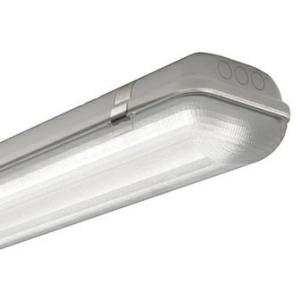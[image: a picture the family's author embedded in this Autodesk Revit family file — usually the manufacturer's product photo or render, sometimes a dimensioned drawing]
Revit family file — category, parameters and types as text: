
# Revit family: 3f_filippi_-_3f_linda_3f_filippi_-_58569_-_3f_linda_led_1x6w_ep_la_l660
name_source: partatom
category: Lighting Fixtures
units: mm (PartAtom-declared; Revit-internal decimal feet)

## family parameters
Cut with Voids When Loaded = No
Host = Face
Light Source = No
Part Type = Normal
Room Calculation Point = No
Round Connector Dimension = Use Diameter
Shared = No

## types (1)
- 3F Filippi - 3F Linda (1 x LED, 1029 lm, 8.5 W, 4000 K)
    Apparent Load = 9 VA
    Approval mark = ENEC
    CIE Flux Codes = 44 77 94 97 100
    Color Rendering = 80
    Color Temperature = 4000 K
    Control Gear = Electronic ballast
    Default Elevation = 1800 mm
    Description = ILLUMINOTECHNICAL
Luminous efficiency 100% (DLOR 97%, ULOR 3%).
Initial luminous flux of the luminaire 1029 lm.
Emergency luminaire luminous flux BLF 57.1%.
Controlled direct symmetric distribution.
Installation Interdistance Transv.D = 1.77 x hu - Long.D = 1.17 x hu.
Tabular UGR (CIE 117 - 4H-8H; S=0.25H; 70/50/20): RUG 18.5 - 18.9.
Beam angle: 109° - 64°.
Luminous efficacy 121 lm/W.
Lifetime (L93/B10): 30000 h. (tq+25°C)
Lifetime (L90/B10): 50000 h. (tq+25°C)
Lifetime (L85/B10): 80000 h. (tq+25°C)
Lifetime (L80/B10): 100000 h. (tq+25°C)
Sudden decreased luminous flux after 50000 hours: 0% (C0).
Photobiological safety in compliance with IEC/TR 62778: RG0 risk exempt, (IEC 62471).
In compliance with IEC/EN 62722-2-1 - IEC/EN 62717 standards.

SOURCE
Linear LED module 6W/840.
Energy efficiency class (UE 2019/2020 - UE 2019/2015): D.
CIE 13.3 Colour rendering index: CRI >80 (R9 <50%).
IES TM-30 Fidelity Index: Rf = 84 Rg = 95.
CCT nominal colour temperature 4000 K.
Colour initial tolerance (MacAdam): SDCM 3.

MECHANICAL
Self-extinguishing V2 polycarbonate housing, injection moulded, RAL 7035 grey.
Ecologic anti-aging injected sealing gasket.
Diffuser in self-extinguishing V2 polycarbonate, photo-engraved interior, UV stabilised, injection moulded with smooth outer surface, tamper-proof opening.
Gear-holder reflector in hot-dip galvanised steel, painted with white polyester base.
Snug fit snap-lock clips for diffuser mounting, in polycarbonate.
Fixing brackets in stainless steel.
Possibility for technicians to access the interior of the luminaire.
Luminaire with limited surface temperature. - D - (EN 60598-2-24)
Dimensions: 660x160 mm, height 100 mm. Weight 2.105 kg.
IP66 protection degree.
Mechanical strength to impacts IK10 (20 joule).
Glow-wire test resistance 850°C.

ELECTRICAL
Halogen Free electronic wiring 230V-50/60Hz, power factor 0.85, THD <25%, constant output current, SELV, class I, 1 driver.
Power of the luminaire 8.5 W.
CE - IEC 60598-1 - EN 60598-1.
EP maintained emergency wiring on board, 1h duration, 24h recharge; compliant with EN 60598-2-22, excluding high risk areas.
SAFE FLICKER: PstLM=<1 and SVM=<0.4 (IEC TR 61547-1 and IEC TR 63158), to ensure a more comfortable and safe light.
Ambient temperature from +5°C to +25°C.
Temperature class T6 max 85°C.
Relative humidity UR: <85%.

INSTALLATION
Ceiling / Suspended / Wall.
All accessories dedicated to this product are available on the Catalog and on our website www.3F-Filippi.com.

APPLICATIONS
Suitable product for food production plants (HACCP), IFS (Food Version 6), BRC (GSFS Food Version 7).
Dry, dusty indoor environments, subject to occasional water splashes.
Virtually shatterproof polycarbonate compatibly with the fumes / atmospheres that compromise the elasticity of plastic materials.
Not suitable for installation on surfaces subject to important vibrations, exposed to weather conditions, on ropes or poles.
Suitable for illumination of public car parks and parking grounds referred to DIN 67528:2018-04.

WARNING
Fixture not suitable for cold stores with an ambient temperature <5°C and/or relative humidity >85%.
Luminaire designed for disposal/recycling at end-of-life.
Replaceable (LED only) light source by a professional. Replaceable control gear by a professional.
    Height = 100 mm  [stored 0.328084 ft]
    Lamp = 1 x LED
    Lamp Light Flux = 1029 lm
    Lamp Power = 8.5 W
    Lamp count = 1
    Length = 660 mm
    Lifetime = 50000 h
    Luminous efficacy = 121 lm/W
    Manufacturer = 3F Filippi
    ModVariant = No
    Model = 3F Filippi - 58569 - 3F Linda LED 1x6W EP LA L660
    Mounting Place = Ceiling
    Mounting Type = Pendant
    Number of Poles = 1
    OnlyDefault = Yes
    Power Factor = 1
    Product Name = 3F Filippi - 3F Linda
    Product group = pendant luminaire
    ProductGroupID = 9
    Protection Class = Protection class I
    Protection Degree = IP 66
    RLX_Detail_Level = 1
    RLX_Emergency_Light_Flux = 0 lm
    RLX_Emergency_Type = 0
    RLX_Emergency_Type_DB = No
    RlxData = <blob elided: 71525 chars, md5=72d27d72>
    Socket = socket
    Standby Power = 0 W
    System Light Flux = 1029 lm
    System Power = 9 W
    Type Comments = Product without accessories
    Type Image = 3ffilippi_58569.jpg
    URL = http://relux.com
    VarID = ---
    Voltage = 0 V
    Weight = 0.00 kg
    Width = 160 mm

note: [stored X ft] marks values corroborated as IEEE doubles in the binary element streams (Revit-internal decimal feet)

## geometry (parser evidence)
native form markers: Blend x4, Sweep x9
no freeform markers — native parametric forms only
